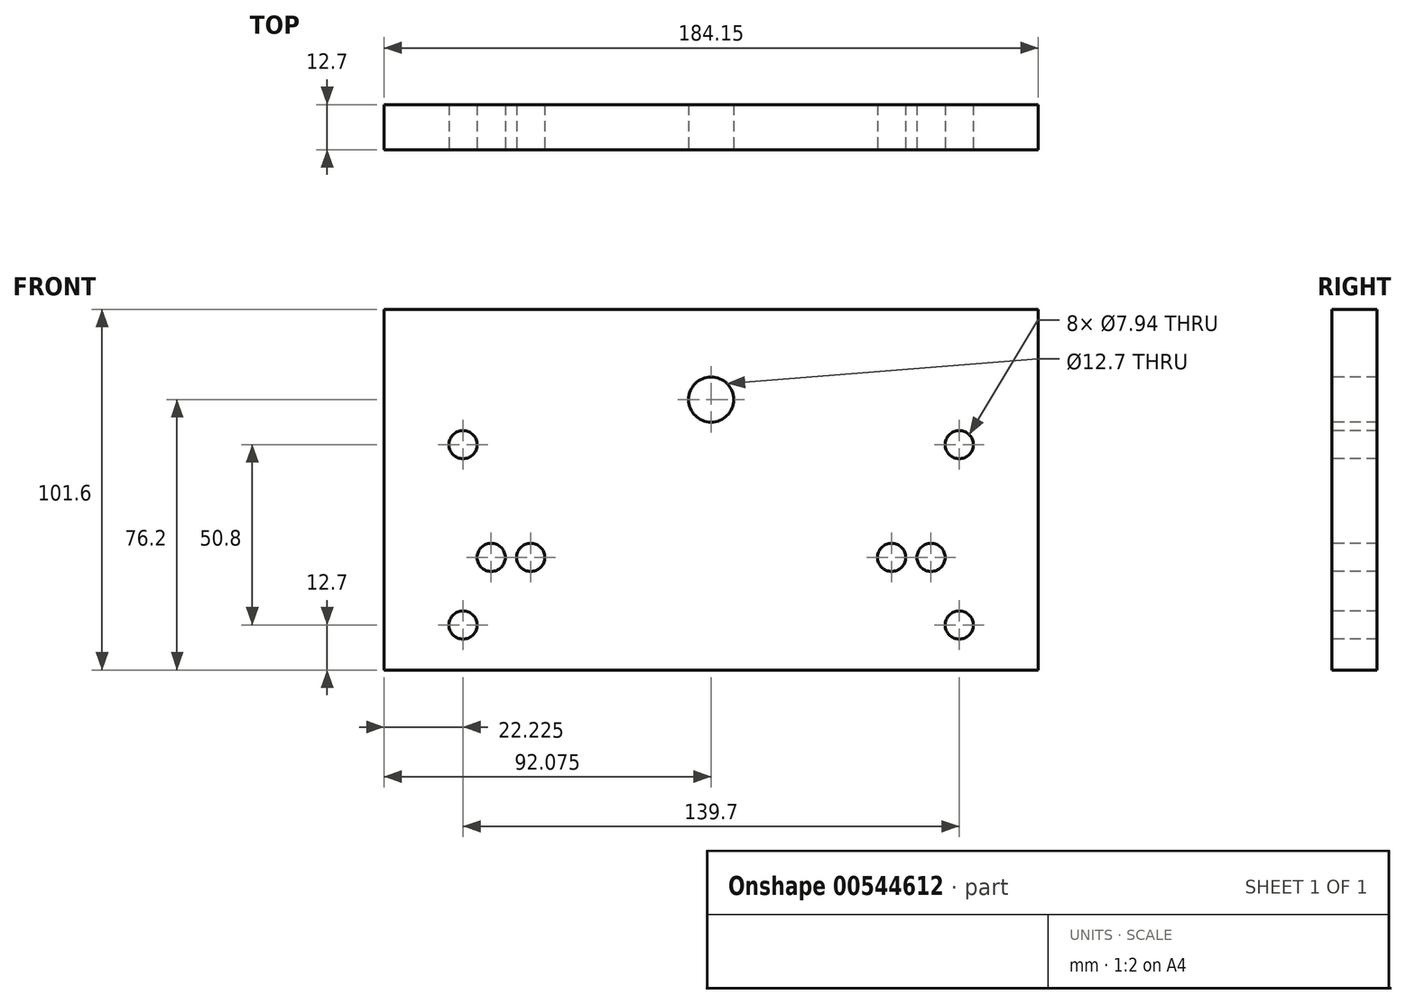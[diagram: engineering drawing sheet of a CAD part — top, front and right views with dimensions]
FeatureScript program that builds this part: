
annotation { "Feature Type Name" : "Feature", "Feature Type Description" : "" }
export const myFeature = defineFeature(function(context is Context, id is Id, definition is map)
    precondition{}
    {
        {
            var Q0;
            Q0=qCreatedBy(makeId("Front.planeOp"),FACE);
            var sketch = newSketch(context, id + "F0", { "sketchPlane" : qUnion([Q0])});
            skLineSegment(sketch, "E0.bottom", {"start": v(0, 0) * mm, "end": v(184.15, 0) * mm});
            skLineSegment(sketch, "E0.top", {"start": v(0, 101.6) * mm, "end": v(184.15, 101.6) * mm});
            skLineSegment(sketch, "E0.left", {"start": v(0, 0) * mm, "end": v(0, 101.6) * mm});
            skLineSegment(sketch, "E0.right", {"start": v(184.15, 0) * mm, "end": v(184.15, 101.6) * mm});
            skSolve(sketch);
        }
        {
            var Q0;
            Q0 = qSketchRegion(id + "F0", true);
            extrude(context, id + "F1", {"entities" : qUnion([Q0]), "depth" : 12.7 * mm, "offsetDistance" : 25.4 * mm});
        }
        {
            var Q0;
            Q0=makeQuery(id+"F1.opExtrude","CAP_FACE",FACE,{"disambiguationData":[OSD([sQuery(id+"F0.wireOp",EDGE,"E0.bottom"),sQuery(id+"F0.wireOp",EDGE,"E0.top"),sQuery(id+"F0.wireOp",EDGE,"E0.left"),sQuery(id+"F0.wireOp",EDGE,"E0.right")])],"isStart":false});
            var sketch = newSketch(context, id + "F2", { "sketchPlane" : qUnion([Q0])});
            skPoint(sketch, "E1", {"position": v(92.08, 76.2) * mm});
            skSolve(sketch);
        }
        {
            var Q0;
            Q0=sQuery(id+"F2.wireOp",VERTEX,"E1");
            var Q1;
            Q1=makeQuery(id+"F1.opExtrude","SWEPT_BODY",BODY,{"disambiguationData":[OSD([sQuery(id+"F0.wireOp",EDGE,"E0.bottom"),sQuery(id+"F0.wireOp",EDGE,"E0.top"),sQuery(id+"F0.wireOp",EDGE,"E0.left"),sQuery(id+"F0.wireOp",EDGE,"E0.right")])]});
            hole(context, id + "F3", {"style" : HoleStyle.SIMPLE, "endStyle" : HoleEndStyle.THROUGH, "holeDiameter" : 12.7 * mm, "majorDiameter" : 6.35 * mm, "isTappedThrough" : true, "tappedDepth" : 12.7 * mm, "tapClearance" : 3, "locations" : qUnion([Q0]), "scope" : qUnion([Q1])});
        }
        {
            var Q0;
            Q0=makeQuery(id+"F1.opExtrude","CAP_FACE",FACE,{"disambiguationData":[OSD([sQuery(id+"F0.wireOp",EDGE,"E0.bottom"),sQuery(id+"F0.wireOp",EDGE,"E0.top"),sQuery(id+"F0.wireOp",EDGE,"E0.left"),sQuery(id+"F0.wireOp",EDGE,"E0.right")])],"isStart":false});
            var sketch = newSketch(context, id + "F4", { "sketchPlane" : qUnion([Q0])});
            skPoint(sketch, "E2", {"position": v(161.93, 63.5) * mm});
            skPoint(sketch, "E3", {"position": v(22.23, 63.5) * mm});
            skPoint(sketch, "E4", {"position": v(197.63, -129.05) * mm});
            skLineSegment(sketch, "E5", {"start": v(92.08, 76.2) * mm, "end": v(92.08, 0) * mm, "construction": true});
            skPoint(sketch, "E6", {"position": v(22.23, 12.7) * mm});
            skPoint(sketch, "E7", {"position": v(161.92, 12.7) * mm});
            skSolve(sketch);
        }
        {
            var Q0;
            Q0=sQuery(id+"F4.wireOp",VERTEX,"E3");
            var Q1;
            Q1=sQuery(id+"F4.wireOp",VERTEX,"E2");
            var Q2;
            Q2=sQuery(id+"F4.wireOp",VERTEX,"E7");
            var Q3;
            Q3=sQuery(id+"F4.wireOp",VERTEX,"E6");
            var Q4;
            Q4=makeQuery(id+"F1.opExtrude","SWEPT_BODY",BODY,{"disambiguationData":[OSD([sQuery(id+"F0.wireOp",EDGE,"E0.bottom"),sQuery(id+"F0.wireOp",EDGE,"E0.top"),sQuery(id+"F0.wireOp",EDGE,"E0.left"),sQuery(id+"F0.wireOp",EDGE,"E0.right")])]});
            hole(context, id + "F5", {"style" : HoleStyle.SIMPLE, "endStyle" : HoleEndStyle.THROUGH, "holeDiameter" : 7.94 * mm, "majorDiameter" : 6.35 * mm, "isTappedThrough" : true, "tappedDepth" : 12.7 * mm, "tapClearance" : 3, "locations" : qUnion([Q0, Q1, Q2, Q3]), "scope" : qUnion([Q4])});
        }
        {
            var Q0;
            Q0=makeQuery(id+"F1.opExtrude","CAP_FACE",FACE,{"disambiguationData":[OSD([sQuery(id+"F0.wireOp",EDGE,"E0.bottom"),sQuery(id+"F0.wireOp",EDGE,"E0.top"),sQuery(id+"F0.wireOp",EDGE,"E0.left"),sQuery(id+"F0.wireOp",EDGE,"E0.right")])],"isStart":false});
            var sketch = newSketch(context, id + "F6", { "sketchPlane" : qUnion([Q0])});
            skPoint(sketch, "E8", {"position": v(41.27, 31.75) * mm});
            skPoint(sketch, "E9", {"position": v(142.88, 31.75) * mm});
            skLineSegment(sketch, "E10", {"start": v(92.08, 76.2) * mm, "end": v(92.08, -25.83) * mm, "construction": true});
            skPoint(sketch, "E11", {"position": v(153.99, 31.75) * mm});
            skPoint(sketch, "E12", {"position": v(30.16, 31.75) * mm});
            skSolve(sketch);
        }
        {
            var Q0;
            Q0=sQuery(id+"F6.wireOp",VERTEX,"E8");
            var Q1;
            Q1=sQuery(id+"F6.wireOp",VERTEX,"E9");
            var Q2;
            Q2=sQuery(id+"F6.wireOp",VERTEX,"E12");
            var Q3;
            Q3=sQuery(id+"F6.wireOp",VERTEX,"E11");
            var Q4;
            Q4=makeQuery(id+"F1.opExtrude","SWEPT_BODY",BODY,{"disambiguationData":[OSD([sQuery(id+"F0.wireOp",EDGE,"E0.bottom"),sQuery(id+"F0.wireOp",EDGE,"E0.top"),sQuery(id+"F0.wireOp",EDGE,"E0.left"),sQuery(id+"F0.wireOp",EDGE,"E0.right")])]});
            hole(context, id + "F7", {"style" : HoleStyle.SIMPLE, "endStyle" : HoleEndStyle.THROUGH, "holeDiameter" : 7.94 * mm, "majorDiameter" : 6.35 * mm, "isTappedThrough" : true, "tappedDepth" : 12.7 * mm, "tapClearance" : 3, "locations" : qUnion([Q0, Q1, Q2, Q3]), "scope" : qUnion([Q4])});
        }
    });
